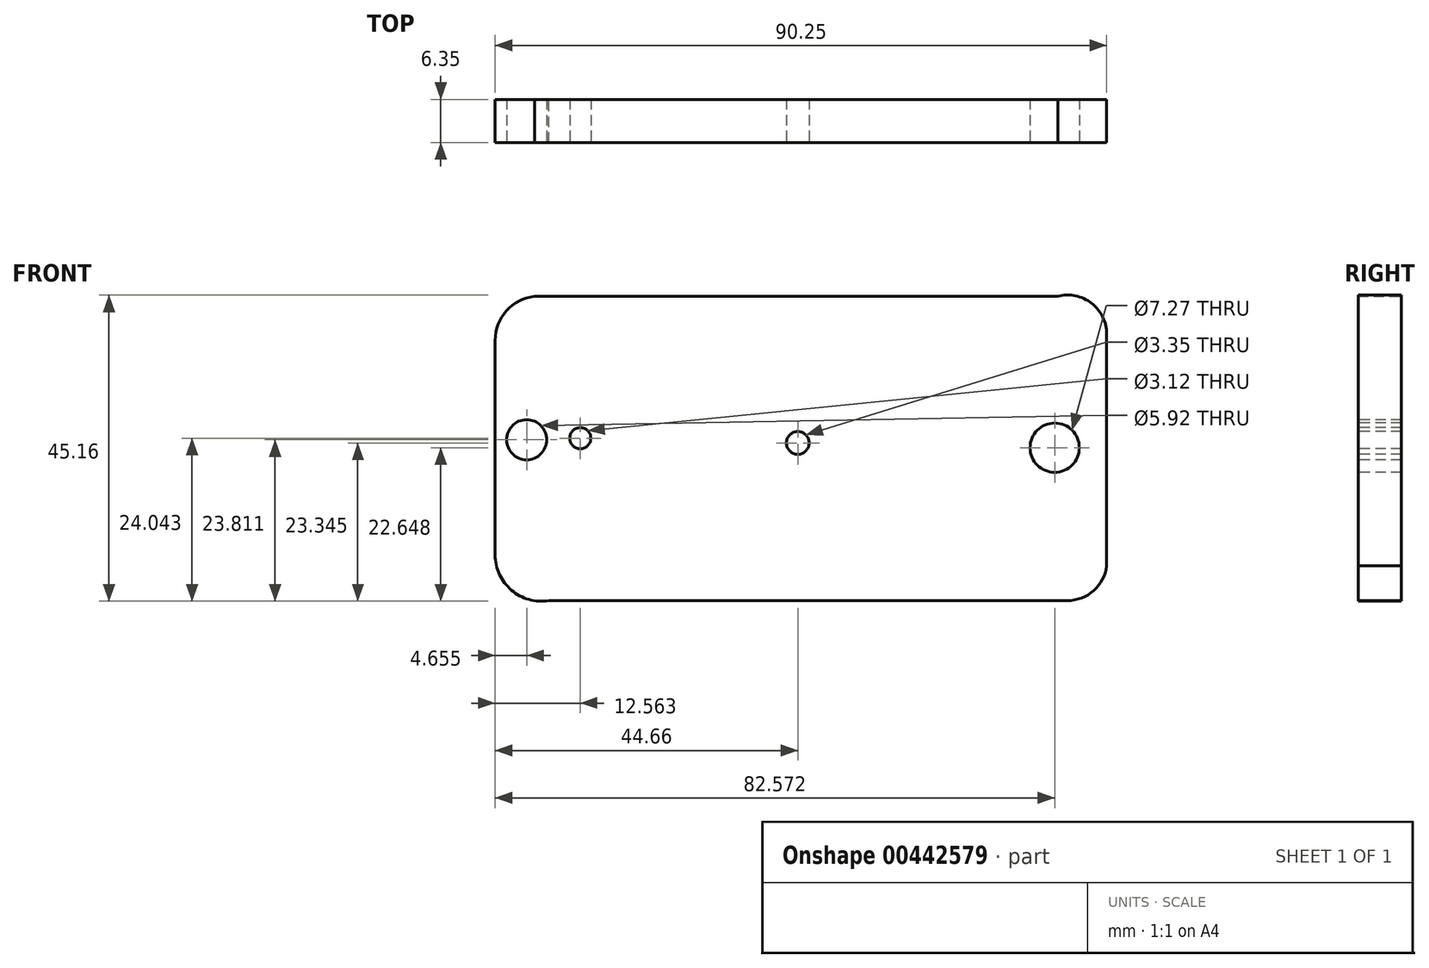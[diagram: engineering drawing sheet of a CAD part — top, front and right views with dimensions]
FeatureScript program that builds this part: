
annotation { "Feature Type Name" : "Feature", "Feature Type Description" : "" }
export const myFeature = defineFeature(function(context is Context, id is Id, definition is map)
    precondition{}
    {
        {
            var Q0;
            Q0=qCreatedBy(makeId("Front.planeOp"),FACE);
            var sketch = newSketch(context, id + "F0", { "sketchPlane" : qUnion([Q0])});
            skLineSegment(sketch, "E0", {"start": v(-44.66, 9.3) * mm, "end": v(-44.66, -22.33) * mm});
            skArc(sketch, "E1", {"start": v(-44.66, -22.33) * mm, "mid": v(-42.26, -27.53) * mm, "end": v(-36.75, -29.07) * mm});
            skArc(sketch, "E2", {"start": v(-44.66, 9.3) * mm, "mid": v(-43, 13.67) * mm, "end": v(-38.84, 15.82) * mm});
            skLineSegment(sketch, "E3", {"start": v(-38.84, 15.82) * mm, "end": v(38.38, 15.82) * mm});
            skArc(sketch, "E4", {"start": v(38.38, 15.82) * mm, "mid": v(41.64, 14.8) * mm, "end": v(43.73, 12.1) * mm});
            skLineSegment(sketch, "E5", {"start": v(43.73, 12.1) * mm, "end": v(43.73, -20.24) * mm});
            skLineSegment(sketch, "E6", {"start": v(-36.75, -29.07) * mm, "end": v(39.77, -29.07) * mm});
            skArc(sketch, "E7", {"start": v(39.77, -29.07) * mm, "mid": v(43.65, -27.61) * mm, "end": v(45.59, -23.96) * mm});
            skLineSegment(sketch, "E8", {"start": v(45.59, -23.96) * mm, "end": v(45.59, 10.23) * mm});
            skArc(sketch, "E9", {"start": v(45.59, 10.23) * mm, "mid": v(43.35, 14.8) * mm, "end": v(38.38, 15.82) * mm});
            skSolve(sketch);
        }
        {
            var Q0;
            Q0=makeQuery(id+"F0.imprint","IMPRINT",FACE,{"disambiguationData":[TD([[makeQuery(id+"F0.imprint","IMPRINT",EDGE,{"derivedFrom":sQuery(id+"F0.wireOp",EDGE,"E0")}),1.0]])]});
            extrude(context, id + "F1", {"entities" : qUnion([Q0]), "depth" : 6.35 * mm});
        }
        {
            var Q0;
            Q0=makeQuery(id+"F1.opExtrude","CAP_FACE",FACE,{"disambiguationData":[OSD([sQuery(id+"F0.wireOp",EDGE,"E0"),sQuery(id+"F0.wireOp",EDGE,"E1"),sQuery(id+"F0.wireOp",EDGE,"E2"),sQuery(id+"F0.wireOp",EDGE,"E3"),sQuery(id+"F0.wireOp",EDGE,"E6"),sQuery(id+"F0.wireOp",EDGE,"E7"),sQuery(id+"F0.wireOp",EDGE,"E8"),sQuery(id+"F0.wireOp",EDGE,"E9")])],"isStart":false});
            var sketch = newSketch(context, id + "F2", { "sketchPlane" : qUnion([Q0])});
            skCircle(sketch, "E10", {"center": v(-40, -5.35) * mm, "radius": 2.96 * mm});
            skCircle(sketch, "E11", {"center": v(-32.1, -5.12) * mm, "radius": 1.56 * mm});
            skCircle(sketch, "E12", {"center": v(0, -5.81) * mm, "radius": 1.68 * mm});
            skCircle(sketch, "E13", {"center": v(37.91, -6.51) * mm, "radius": 3.63 * mm});
            skPoint(sketch, "E13.centerSnap0", {"position": v(-44.66, -6.51) * mm});
            skSolve(sketch);
        }
        {
            var Q0;
            Q0=makeQuery(id+"F2.imprint","IMPRINT",FACE,{"disambiguationData":[TD([[makeQuery(id+"F2.imprint","IMPRINT",EDGE,{"derivedFrom":sQuery(id+"F2.wireOp",EDGE,"E10")}),1.0]])]});
            var Q1;
            Q1=makeQuery(id+"F2.imprint","IMPRINT",FACE,{"disambiguationData":[TD([[makeQuery(id+"F2.imprint","IMPRINT",EDGE,{"derivedFrom":sQuery(id+"F2.wireOp",EDGE,"E11")}),1.0]])]});
            var Q2;
            Q2=makeQuery(id+"F2.imprint","IMPRINT",FACE,{"disambiguationData":[TD([[makeQuery(id+"F2.imprint","IMPRINT",EDGE,{"derivedFrom":sQuery(id+"F2.wireOp",EDGE,"E12")}),1.0]])]});
            var Q3;
            Q3=makeQuery(id+"F2.imprint","IMPRINT",FACE,{"disambiguationData":[TD([[makeQuery(id+"F2.imprint","IMPRINT",EDGE,{"derivedFrom":sQuery(id+"F2.wireOp",EDGE,"E13")}),1.0]])]});
            extrude(context, id + "F3", {"entities" : qUnion([Q0, Q1, Q2, Q3]), "operationType" : NewBodyOperationType.REMOVE, "oppositeDirection" : true, "depth" : 25.4 * mm});
        }
    });
